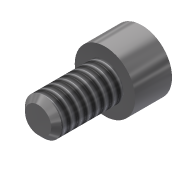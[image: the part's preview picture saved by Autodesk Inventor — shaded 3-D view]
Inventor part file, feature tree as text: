
AUTODESK INVENTOR PART (.ipt)
format: ipt  version: 2013 (Build 170138000, 138)  size: 107,008 bytes
history: native  units: in
note: dims shown in document units (in); Inventor stores cm internally (conversion verified against a paired STEP export)
features: extrude x3, sketch x3, thread x1, chamfer x1
ambient origin geometry x8: Origin, YZ Plane, XZ Plane, XY Plane, X Axis, Y Axis, Z Axis, Center Point
bodies: Solid1 (feature_tree)
feature tree (8):
  extrude  "Extrusion1"  Depth=0.25in TaperAngle=0.0deg
  extrude  "Extrusion2"  Depth=0.138in TaperAngle=0.0deg
  extrude  "Extrusion3"  Depth=0.069in TaperAngle=0.0deg
  thread  "Thread1"  [1 undecoded]
  chamfer  "Chamfer1"  Distance=0.02in Angle=45.0deg
  sketch  "Sketch1"  dims[d0=0.138in d1=0.25in d2=0.0in]
  sketch  "Sketch2"  dims[d3=0.226in d4=0.138in d5=0.0in]
  sketch  "Sketch3"  dims[d6=0.1094in d7=0.069in d8=0.0in d9=1.0in d10=0.0in d11=0.02in d12=0.125in d13=45.0deg]
note: 1 required parameter value undecoded (feature->parameter linkage not recoverable at this tier; creation-order binding heuristic only, values carry confidence <= 0.55)
